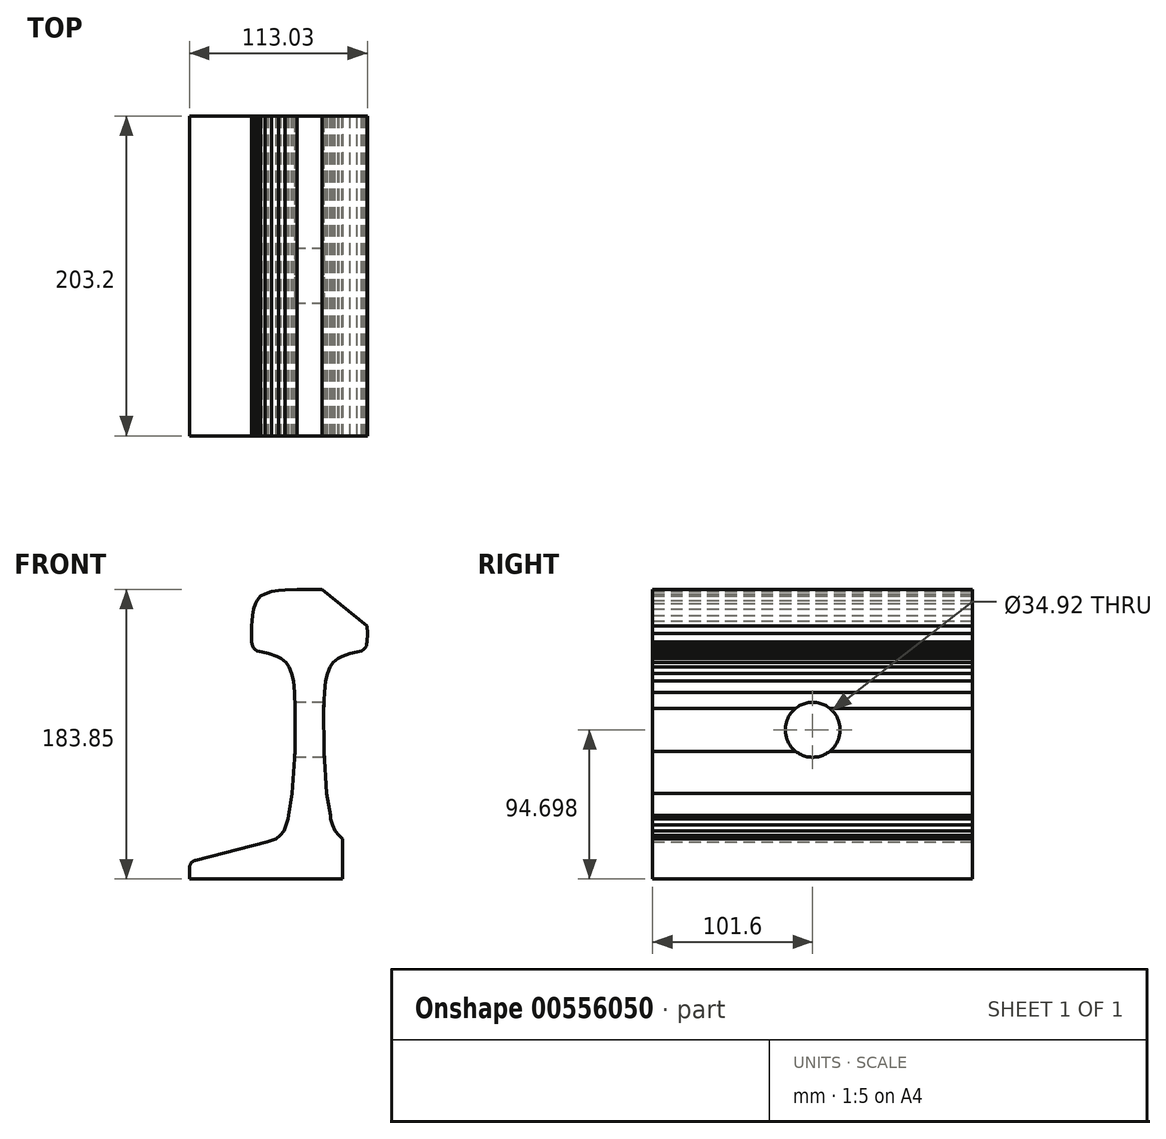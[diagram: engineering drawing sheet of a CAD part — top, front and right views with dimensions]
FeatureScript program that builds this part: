
annotation { "Feature Type Name" : "Feature", "Feature Type Description" : "" }
export const myFeature = defineFeature(function(context is Context, id is Id, definition is map)
    precondition{}
    {
        {
            var Q0;
            Q0=qCreatedBy(makeId("Front.planeOp"),FACE);
            var sketch = newSketch(context, id + "F0", { "sketchPlane" : qUnion([Q0])});
            skLineSegment(sketch, "E0", {"start": v(-76.2, -57.1) * mm, "end": v(76.2, -57.1) * mm});
            skLineSegment(sketch, "E1", {"start": v(-76.2, -57.1) * mm, "end": v(-76.2, -46.22) * mm});
            skLineSegment(sketch, "E2", {"start": v(-26.84, -33.73) * mm, "end": v(-76.2, -46.22) * mm});
            skPoint(sketch, "E3.startSnap0", {"position": v(0, -57.1) * mm});
            skPoint(sketch, "E3.endSnap0", {"position": v(0, -57.1) * mm});
            skLineSegment(sketch, "E4.MirrorCS", {"start": v(26.84, -33.73) * mm, "end": v(76.2, -46.22) * mm});
            skLineSegment(sketch, "E5.MirrorCS", {"start": v(0, -26.94) * mm, "end": v(0, -26.94) * mm});
            skLineSegment(sketch, "E6.MirrorCS", {"start": v(76.2, -57.1) * mm, "end": v(76.2, -46.22) * mm});
            skLineSegment(sketch, "E7", {"start": v(-26.84, -33.73) * mm, "end": v(-21.16, -31.84) * mm});
            skLineSegment(sketch, "E8", {"start": v(-21.16, -31.84) * mm, "end": v(-18.7, -29.61) * mm});
            skLineSegment(sketch, "E9", {"start": v(-18.7, -29.61) * mm, "end": v(-16.22, -26.55) * mm});
            skLineSegment(sketch, "E10", {"start": v(-16.22, -26.55) * mm, "end": v(-14.69, -22.9) * mm});
            skLineSegment(sketch, "E11", {"start": v(-14.69, -22.9) * mm, "end": v(-13.49, -19.14) * mm});
            skLineSegment(sketch, "E12", {"start": v(-13.49, -19.14) * mm, "end": v(-13.3, -16.85) * mm});
            skLineSegment(sketch, "E13", {"start": v(-13.3, -16.85) * mm, "end": v(-10.94, -2.66) * mm});
            skLineSegment(sketch, "E14", {"start": v(-10.94, -2.66) * mm, "end": v(-9.17, 23.94) * mm});
            skLineSegment(sketch, "E15", {"start": v(-9.17, 23.94) * mm, "end": v(-9.1, 51.27) * mm});
            skLineSegment(sketch, "E16", {"start": v(-9.1, 51.27) * mm, "end": v(-9.47, 61.37) * mm});
            skLineSegment(sketch, "E17", {"start": v(-36.63, 93.52) * mm, "end": v(-36.6, 93.52) * mm});
            skLineSegment(sketch, "E18", {"start": v(-9.47, 61.37) * mm, "end": v(-10.2, 68.53) * mm});
            skLineSegment(sketch, "E19", {"start": v(-10.2, 68.53) * mm, "end": v(-11.42, 73.4) * mm});
            skLineSegment(sketch, "E20", {"start": v(-11.42, 73.4) * mm, "end": v(-12.99, 77.66) * mm});
            skLineSegment(sketch, "E21", {"start": v(-12.99, 77.66) * mm, "end": v(-14.98, 80.45) * mm});
            skLineSegment(sketch, "E22", {"start": v(-14.98, 80.45) * mm, "end": v(-18.1, 83) * mm});
            skLineSegment(sketch, "E23", {"start": v(-18.1, 83) * mm, "end": v(-20.68, 84.15) * mm});
            skLineSegment(sketch, "E24", {"start": v(-20.68, 84.15) * mm, "end": v(-25.92, 85.98) * mm});
            skLineSegment(sketch, "E25", {"start": v(-25.92, 85.98) * mm, "end": v(-30.18, 87.13) * mm});
            skLineSegment(sketch, "E26", {"start": v(-30.18, 87.13) * mm, "end": v(-33.1, 87.75) * mm});
            skLineSegment(sketch, "E27", {"start": v(-33.1, 87.75) * mm, "end": v(-34.18, 88.3) * mm});
            skLineSegment(sketch, "E28", {"start": v(-34.18, 88.3) * mm, "end": v(-35.39, 89.62) * mm});
            skLineSegment(sketch, "E29", {"start": v(-35.39, 89.62) * mm, "end": v(-36.17, 91) * mm});
            skLineSegment(sketch, "E30", {"start": v(-36.17, 91) * mm, "end": v(-36.4, 91.97) * mm});
            skLineSegment(sketch, "E31", {"start": v(-36.4, 91.97) * mm, "end": v(-36.6, 93.51) * mm});
            skLineSegment(sketch, "E32", {"start": v(-36.6, 93.51) * mm, "end": v(-36.83, 98.88) * mm});
            skLineSegment(sketch, "E33", {"start": v(-36.83, 98.88) * mm, "end": v(-36.67, 103.67) * mm});
            skLineSegment(sketch, "E34", {"start": v(-36.67, 103.67) * mm, "end": v(-36.4, 106.65) * mm});
            skLineSegment(sketch, "E35", {"start": v(-36.4, 106.65) * mm, "end": v(-36.18, 110.32) * mm});
            skLineSegment(sketch, "E36", {"start": v(-36.18, 110.32) * mm, "end": v(-35.56, 114.28) * mm});
            skLineSegment(sketch, "E37", {"start": v(-35.56, 114.28) * mm, "end": v(-34.24, 117.98) * mm});
            skLineSegment(sketch, "E38", {"start": v(-34.24, 117.98) * mm, "end": v(-33.33, 119.88) * mm});
            skLineSegment(sketch, "E39", {"start": v(-33.33, 119.88) * mm, "end": v(-31.13, 122.46) * mm});
            skLineSegment(sketch, "E40", {"start": v(-31.13, 122.46) * mm, "end": v(-28.22, 124.04) * mm});
            skLineSegment(sketch, "E41", {"start": v(-28.22, 124.04) * mm, "end": v(-24.03, 125.35) * mm});
            skLineSegment(sketch, "E42", {"start": v(-24.03, 125.35) * mm, "end": v(-19.54, 126) * mm});
            skLineSegment(sketch, "E43.MirrorCS", {"start": v(36.4, 91.97) * mm, "end": v(36.6, 93.51) * mm});
            skLineSegment(sketch, "E44.MirrorCS", {"start": v(36.17, 91) * mm, "end": v(36.4, 91.97) * mm});
            skLineSegment(sketch, "E45.MirrorCS", {"start": v(13.49, -19.14) * mm, "end": v(13.3, -16.85) * mm});
            skLineSegment(sketch, "E46.MirrorCS", {"start": v(36.67, 103.67) * mm, "end": v(36.4, 106.65) * mm});
            skLineSegment(sketch, "E47.MirrorCS", {"start": v(20.68, 84.15) * mm, "end": v(25.92, 85.98) * mm});
            skLineSegment(sketch, "E48.MirrorCS", {"start": v(31.13, 122.46) * mm, "end": v(28.22, 124.04) * mm});
            skLineSegment(sketch, "E49.MirrorCS", {"start": v(36.6, 93.51) * mm, "end": v(36.83, 98.88) * mm});
            skLineSegment(sketch, "E50.MirrorCS", {"start": v(16.22, -26.55) * mm, "end": v(14.69, -22.9) * mm});
            skLineSegment(sketch, "E51.MirrorCS", {"start": v(34.18, 88.3) * mm, "end": v(35.39, 89.62) * mm});
            skLineSegment(sketch, "E52.MirrorCS", {"start": v(14.69, -22.9) * mm, "end": v(13.49, -19.14) * mm});
            skLineSegment(sketch, "E53.MirrorCS", {"start": v(12.99, 77.66) * mm, "end": v(14.98, 80.45) * mm});
            skLineSegment(sketch, "E54.MirrorCS", {"start": v(35.56, 114.28) * mm, "end": v(34.24, 117.98) * mm});
            skLineSegment(sketch, "E55.MirrorCS", {"start": v(28.22, 124.04) * mm, "end": v(24.03, 125.35) * mm});
            skLineSegment(sketch, "E56.MirrorCS", {"start": v(25.92, 85.98) * mm, "end": v(30.18, 87.13) * mm});
            skLineSegment(sketch, "E57.MirrorCS", {"start": v(26.84, -33.73) * mm, "end": v(21.16, -31.84) * mm});
            skLineSegment(sketch, "E58.MirrorCS", {"start": v(18.1, 83) * mm, "end": v(20.68, 84.15) * mm});
            skLineSegment(sketch, "E59.MirrorCS", {"start": v(21.16, -31.84) * mm, "end": v(18.7, -29.61) * mm});
            skLineSegment(sketch, "E60.MirrorCS", {"start": v(14.98, 80.45) * mm, "end": v(18.1, 83) * mm});
            skLineSegment(sketch, "E61.MirrorCS", {"start": v(33.1, 87.75) * mm, "end": v(34.18, 88.3) * mm});
            skLineSegment(sketch, "E62.MirrorCS", {"start": v(33.33, 119.88) * mm, "end": v(31.13, 122.46) * mm});
            skLineSegment(sketch, "E63.MirrorCS", {"start": v(30.18, 87.13) * mm, "end": v(33.1, 87.75) * mm});
            skLineSegment(sketch, "E64.MirrorCS", {"start": v(10.2, 68.53) * mm, "end": v(11.42, 73.4) * mm});
            skLineSegment(sketch, "E65.MirrorCS", {"start": v(34.24, 117.98) * mm, "end": v(33.33, 119.88) * mm});
            skLineSegment(sketch, "E66.MirrorCS", {"start": v(11.42, 73.4) * mm, "end": v(12.99, 77.66) * mm});
            skLineSegment(sketch, "E67.MirrorCS", {"start": v(24.03, 125.35) * mm, "end": v(19.54, 126) * mm});
            skLineSegment(sketch, "E68.MirrorCS", {"start": v(18.7, -29.61) * mm, "end": v(16.22, -26.55) * mm});
            skLineSegment(sketch, "E69.MirrorCS", {"start": v(35.39, 89.62) * mm, "end": v(36.17, 91) * mm});
            skLineSegment(sketch, "E70.MirrorCS", {"start": v(36.18, 110.32) * mm, "end": v(35.56, 114.28) * mm});
            skLineSegment(sketch, "E71.MirrorCS", {"start": v(36.4, 106.65) * mm, "end": v(36.18, 110.32) * mm});
            skLineSegment(sketch, "E72.MirrorCS", {"start": v(9.47, 61.37) * mm, "end": v(10.2, 68.53) * mm});
            skLineSegment(sketch, "E73.MirrorCS", {"start": v(15.45, 126.6) * mm, "end": v(15.43, 126.61) * mm});
            skLineSegment(sketch, "E74.MirrorCS", {"start": v(36.83, 98.88) * mm, "end": v(36.67, 103.67) * mm});
            skLineSegment(sketch, "E75.MirrorCS", {"start": v(10.94, -2.66) * mm, "end": v(9.17, 23.94) * mm});
            skLineSegment(sketch, "E76.MirrorCS", {"start": v(9.1, 51.27) * mm, "end": v(9.47, 61.37) * mm});
            skLineSegment(sketch, "E77.MirrorCS", {"start": v(13.3, -16.85) * mm, "end": v(10.94, -2.66) * mm});
            skLineSegment(sketch, "E78.MirrorCS", {"start": v(9.17, 23.94) * mm, "end": v(9.1, 51.27) * mm});
            skPoint(sketch, "E79.start.orphan", {"position": v(-15.43, 126.61) * mm});
            skLineSegment(sketch, "E80", {"start": v(-19.54, 126) * mm, "end": v(-15.43, 126.4) * mm});
            skLineSegment(sketch, "E81", {"start": v(-15.43, 126.4) * mm, "end": v(-8, 126.76) * mm});
            skLineSegment(sketch, "E82", {"start": v(-8, 126.76) * mm, "end": v(0, 126.76) * mm});
            skLineSegment(sketch, "E83.MirrorCS", {"start": v(8, 126.76) * mm, "end": v(0, 126.76) * mm});
            skLineSegment(sketch, "E84.MirrorCS", {"start": v(15.43, 126.4) * mm, "end": v(8, 126.76) * mm});
            skLineSegment(sketch, "E85.MirrorCS", {"start": v(19.54, 126) * mm, "end": v(15.43, 126.4) * mm});
            skPoint(sketch, "E86.orphan", {"position": v(-76.2, -26.94) * mm});
            skPoint(sketch, "E87.orphan", {"position": v(-31.72, -14.5) * mm});
            skPoint(sketch, "E88.end.orphan", {"position": v(-76.21, 41.14) * mm});
            skPoint(sketch, "E88.start.orphan", {"position": v(-76.21, -8.79) * mm});
            skLineSegment(sketch, "E89", {"start": v(76.2, -57.1) * mm, "end": v(76.2, -57.1) * mm});
            skPoint(sketch, "E90.orphan", {"position": v(76.2, -26.94) * mm});
            skPoint(sketch, "E91.MirrorCS.end.orphan", {"position": v(76.21, -8.79) * mm});
            skPoint(sketch, "E91.MirrorCS.start.orphan", {"position": v(31.72, -14.5) * mm});
            skPoint(sketch, "E92.orphan", {"position": v(0, -26.94) * mm});
            skLineSegment(sketch, "E93.trimOffspring", {"start": v(36.6, 93.52) * mm, "end": v(37.03, 93.52) * mm});
            skPoint(sketch, "E94.trimOffspring.end.orphan", {"position": v(0, 152.1) * mm});
            skPoint(sketch, "E3.start.orphan", {"position": v(0, -57.1) * mm});
            skSolve(sketch);
        }
        {
            var Q0;
            Q0=qSketchRegion(id+"F0",true);
            extrude(context, id + "F1", {"entities" : qUnion([Q0]), "depth" : 203.2 * mm, "offsetDistance" : 25.4 * mm});
        }
        {
            var Q0;
            Q0=makeQuery(id+"F1.opExtrude","SWEPT_EDGE",EDGE,{"disambiguationData":[OSD([sQuery(id+"F0.wireOp",EDGE,"E4.MirrorCS"),sQuery(id+"F0.wireOp",EDGE,"E6.MirrorCS")])]});
            var Q1;
            Q1=makeQuery(id+"F1.opExtrude","SWEPT_EDGE",EDGE,{"disambiguationData":[OSD([sQuery(id+"F0.wireOp",EDGE,"E1"),sQuery(id+"F0.wireOp",EDGE,"E2")])]});
            fillet(context, id + "F2", {"entities" : qUnion([Q0, Q1]), "radius" : 5.08 * mm, "tangentPropagation" : true, "allowEdgeOverflow" : false});
        }
        {
            var Q0;
            Q0=makeQuery(id+"F1.opExtrude","CAP_FACE",FACE,{"disambiguationData":[OSD([sQuery(id+"F0.wireOp",EDGE,"E0"),sQuery(id+"F0.wireOp",EDGE,"E1"),sQuery(id+"F0.wireOp",EDGE,"E2"),sQuery(id+"F0.wireOp",EDGE,"E4.MirrorCS"),sQuery(id+"F0.wireOp",EDGE,"E7"),sQuery(id+"F0.wireOp",EDGE,"E8"),sQuery(id+"F0.wireOp",EDGE,"E9"),sQuery(id+"F0.wireOp",EDGE,"E10"),sQuery(id+"F0.wireOp",EDGE,"E11"),sQuery(id+"F0.wireOp",EDGE,"E12"),sQuery(id+"F0.wireOp",EDGE,"E13"),sQuery(id+"F0.wireOp",EDGE,"E14"),sQuery(id+"F0.wireOp",EDGE,"E15"),sQuery(id+"F0.wireOp",EDGE,"E16"),sQuery(id+"F0.wireOp",EDGE,"E18"),sQuery(id+"F0.wireOp",EDGE,"E19"),sQuery(id+"F0.wireOp",EDGE,"E20"),sQuery(id+"F0.wireOp",EDGE,"E21"),sQuery(id+"F0.wireOp",EDGE,"E22"),sQuery(id+"F0.wireOp",EDGE,"E23"),sQuery(id+"F0.wireOp",EDGE,"E24"),sQuery(id+"F0.wireOp",EDGE,"E25"),sQuery(id+"F0.wireOp",EDGE,"E26"),sQuery(id+"F0.wireOp",EDGE,"E27"),sQuery(id+"F0.wireOp",EDGE,"E28"),sQuery(id+"F0.wireOp",EDGE,"E29"),sQuery(id+"F0.wireOp",EDGE,"E30"),sQuery(id+"F0.wireOp",EDGE,"E31"),sQuery(id+"F0.wireOp",EDGE,"E32"),sQuery(id+"F0.wireOp",EDGE,"E33"),sQuery(id+"F0.wireOp",EDGE,"E34"),sQuery(id+"F0.wireOp",EDGE,"E35"),sQuery(id+"F0.wireOp",EDGE,"E36"),sQuery(id+"F0.wireOp",EDGE,"E37"),sQuery(id+"F0.wireOp",EDGE,"E38"),sQuery(id+"F0.wireOp",EDGE,"E39"),sQuery(id+"F0.wireOp",EDGE,"E40"),sQuery(id+"F0.wireOp",EDGE,"E41"),sQuery(id+"F0.wireOp",EDGE,"E42"),sQuery(id+"F0.wireOp",EDGE,"E43.MirrorCS"),sQuery(id+"F0.wireOp",EDGE,"E44.MirrorCS"),sQuery(id+"F0.wireOp",EDGE,"E45.MirrorCS"),sQuery(id+"F0.wireOp",EDGE,"E46.MirrorCS"),sQuery(id+"F0.wireOp",EDGE,"E47.MirrorCS"),sQuery(id+"F0.wireOp",EDGE,"E48.MirrorCS"),sQuery(id+"F0.wireOp",EDGE,"E49.MirrorCS"),sQuery(id+"F0.wireOp",EDGE,"E50.MirrorCS"),sQuery(id+"F0.wireOp",EDGE,"E51.MirrorCS"),sQuery(id+"F0.wireOp",EDGE,"E52.MirrorCS"),sQuery(id+"F0.wireOp",EDGE,"E53.MirrorCS"),sQuery(id+"F0.wireOp",EDGE,"E54.MirrorCS"),sQuery(id+"F0.wireOp",EDGE,"E55.MirrorCS"),sQuery(id+"F0.wireOp",EDGE,"E56.MirrorCS"),sQuery(id+"F0.wireOp",EDGE,"E57.MirrorCS"),sQuery(id+"F0.wireOp",EDGE,"E58.MirrorCS"),sQuery(id+"F0.wireOp",EDGE,"E59.MirrorCS"),sQuery(id+"F0.wireOp",EDGE,"E60.MirrorCS"),sQuery(id+"F0.wireOp",EDGE,"E61.MirrorCS"),sQuery(id+"F0.wireOp",EDGE,"E62.MirrorCS"),sQuery(id+"F0.wireOp",EDGE,"E63.MirrorCS"),sQuery(id+"F0.wireOp",EDGE,"E64.MirrorCS"),sQuery(id+"F0.wireOp",EDGE,"E65.MirrorCS"),sQuery(id+"F0.wireOp",EDGE,"E66.MirrorCS"),sQuery(id+"F0.wireOp",EDGE,"E67.MirrorCS"),sQuery(id+"F0.wireOp",EDGE,"E68.MirrorCS"),sQuery(id+"F0.wireOp",EDGE,"E69.MirrorCS"),sQuery(id+"F0.wireOp",EDGE,"E70.MirrorCS"),sQuery(id+"F0.wireOp",EDGE,"E71.MirrorCS"),sQuery(id+"F0.wireOp",EDGE,"E72.MirrorCS"),sQuery(id+"F0.wireOp",EDGE,"E74.MirrorCS"),sQuery(id+"F0.wireOp",EDGE,"E75.MirrorCS"),sQuery(id+"F0.wireOp",EDGE,"E6.MirrorCS"),sQuery(id+"F0.wireOp",EDGE,"E76.MirrorCS"),sQuery(id+"F0.wireOp",EDGE,"E77.MirrorCS"),sQuery(id+"F0.wireOp",EDGE,"E78.MirrorCS"),sQuery(id+"F0.wireOp",EDGE,"E80"),sQuery(id+"F0.wireOp",EDGE,"E81"),sQuery(id+"F0.wireOp",EDGE,"E82"),sQuery(id+"F0.wireOp",EDGE,"E83.MirrorCS"),sQuery(id+"F0.wireOp",EDGE,"E84.MirrorCS"),sQuery(id+"F0.wireOp",EDGE,"E85.MirrorCS")])],"isStart":false});
            var sketch = newSketch(context, id + "F3", { "sketchPlane" : qUnion([Q0])});
            skLineSegment(sketch, "E95", {"start": v(21.16, -31.84) * mm, "end": v(21.16, -57.1) * mm});
            skSolve(sketch);
        }
        {
            var Q0;
            {var subQ4=sQuery(id+"F3.wireOp",EDGE,"E95");Q0=makeQuery(id+"F3.imprint","IMPRINT",FACE,{"disambiguationData":[TD([[makeQuery(id+"F3.imprint","IMPRINT",EDGE,{"derivedFrom":subQ4}),1.0]])]});}
            extrude(context, id + "F4", {"entities" : qUnion([Q0]), "operationType" : NewBodyOperationType.REMOVE, "oppositeDirection" : true, "depth" : 508 * mm, "offsetDistance" : 25.4 * mm});
        }
        {
            var Q0;
            Q0=qCreatedBy(makeId("Right.planeOp"),FACE);
            var sketch = newSketch(context, id + "F5", { "sketchPlane" : qUnion([Q0])});
            skPoint(sketch, "E96.centerSnap0", {"position": v(0, 37.6) * mm});
            skPoint(sketch, "E96.centerSnap1", {"position": v(-101.6, 23.94) * mm});
            skCircle(sketch, "E97", {"center": v(-101.6, 37.6) * mm, "radius": 17.46 * mm});
            skSolve(sketch);
        }
        {
            var Q0;
            Q0 = qSketchRegion(id + "F5", true);
            extrude(context, id + "F6", {"entities" : qUnion([Q0]), "operationType" : NewBodyOperationType.REMOVE, "endBound" : BoundingType.SYMMETRIC, "depth" : 304.8 * mm, "offsetDistance" : 25.4 * mm});
        }
        {
            var Q0;
            Q0=makeQuery(id+"F1.opExtrude","CAP_FACE",FACE,{"disambiguationData":[OSD([sQuery(id+"F0.wireOp",EDGE,"E0"),sQuery(id+"F0.wireOp",EDGE,"E1"),sQuery(id+"F0.wireOp",EDGE,"E2"),sQuery(id+"F0.wireOp",EDGE,"E4.MirrorCS"),sQuery(id+"F0.wireOp",EDGE,"E7"),sQuery(id+"F0.wireOp",EDGE,"E8"),sQuery(id+"F0.wireOp",EDGE,"E9"),sQuery(id+"F0.wireOp",EDGE,"E10"),sQuery(id+"F0.wireOp",EDGE,"E11"),sQuery(id+"F0.wireOp",EDGE,"E12"),sQuery(id+"F0.wireOp",EDGE,"E13"),sQuery(id+"F0.wireOp",EDGE,"E14"),sQuery(id+"F0.wireOp",EDGE,"E15"),sQuery(id+"F0.wireOp",EDGE,"E16"),sQuery(id+"F0.wireOp",EDGE,"E18"),sQuery(id+"F0.wireOp",EDGE,"E19"),sQuery(id+"F0.wireOp",EDGE,"E20"),sQuery(id+"F0.wireOp",EDGE,"E21"),sQuery(id+"F0.wireOp",EDGE,"E22"),sQuery(id+"F0.wireOp",EDGE,"E23"),sQuery(id+"F0.wireOp",EDGE,"E24"),sQuery(id+"F0.wireOp",EDGE,"E25"),sQuery(id+"F0.wireOp",EDGE,"E26"),sQuery(id+"F0.wireOp",EDGE,"E27"),sQuery(id+"F0.wireOp",EDGE,"E28"),sQuery(id+"F0.wireOp",EDGE,"E29"),sQuery(id+"F0.wireOp",EDGE,"E30"),sQuery(id+"F0.wireOp",EDGE,"E31"),sQuery(id+"F0.wireOp",EDGE,"E32"),sQuery(id+"F0.wireOp",EDGE,"E33"),sQuery(id+"F0.wireOp",EDGE,"E34"),sQuery(id+"F0.wireOp",EDGE,"E35"),sQuery(id+"F0.wireOp",EDGE,"E36"),sQuery(id+"F0.wireOp",EDGE,"E37"),sQuery(id+"F0.wireOp",EDGE,"E38"),sQuery(id+"F0.wireOp",EDGE,"E39"),sQuery(id+"F0.wireOp",EDGE,"E40"),sQuery(id+"F0.wireOp",EDGE,"E41"),sQuery(id+"F0.wireOp",EDGE,"E42"),sQuery(id+"F0.wireOp",EDGE,"E43.MirrorCS"),sQuery(id+"F0.wireOp",EDGE,"E44.MirrorCS"),sQuery(id+"F0.wireOp",EDGE,"E45.MirrorCS"),sQuery(id+"F0.wireOp",EDGE,"E46.MirrorCS"),sQuery(id+"F0.wireOp",EDGE,"E47.MirrorCS"),sQuery(id+"F0.wireOp",EDGE,"E48.MirrorCS"),sQuery(id+"F0.wireOp",EDGE,"E49.MirrorCS"),sQuery(id+"F0.wireOp",EDGE,"E50.MirrorCS"),sQuery(id+"F0.wireOp",EDGE,"E51.MirrorCS"),sQuery(id+"F0.wireOp",EDGE,"E52.MirrorCS"),sQuery(id+"F0.wireOp",EDGE,"E53.MirrorCS"),sQuery(id+"F0.wireOp",EDGE,"E54.MirrorCS"),sQuery(id+"F0.wireOp",EDGE,"E55.MirrorCS"),sQuery(id+"F0.wireOp",EDGE,"E56.MirrorCS"),sQuery(id+"F0.wireOp",EDGE,"E57.MirrorCS"),sQuery(id+"F0.wireOp",EDGE,"E58.MirrorCS"),sQuery(id+"F0.wireOp",EDGE,"E59.MirrorCS"),sQuery(id+"F0.wireOp",EDGE,"E60.MirrorCS"),sQuery(id+"F0.wireOp",EDGE,"E61.MirrorCS"),sQuery(id+"F0.wireOp",EDGE,"E62.MirrorCS"),sQuery(id+"F0.wireOp",EDGE,"E63.MirrorCS"),sQuery(id+"F0.wireOp",EDGE,"E64.MirrorCS"),sQuery(id+"F0.wireOp",EDGE,"E65.MirrorCS"),sQuery(id+"F0.wireOp",EDGE,"E66.MirrorCS"),sQuery(id+"F0.wireOp",EDGE,"E67.MirrorCS"),sQuery(id+"F0.wireOp",EDGE,"E68.MirrorCS"),sQuery(id+"F0.wireOp",EDGE,"E69.MirrorCS"),sQuery(id+"F0.wireOp",EDGE,"E70.MirrorCS"),sQuery(id+"F0.wireOp",EDGE,"E71.MirrorCS"),sQuery(id+"F0.wireOp",EDGE,"E72.MirrorCS"),sQuery(id+"F0.wireOp",EDGE,"E74.MirrorCS"),sQuery(id+"F0.wireOp",EDGE,"E75.MirrorCS"),sQuery(id+"F0.wireOp",EDGE,"E6.MirrorCS"),sQuery(id+"F0.wireOp",EDGE,"E76.MirrorCS"),sQuery(id+"F0.wireOp",EDGE,"E77.MirrorCS"),sQuery(id+"F0.wireOp",EDGE,"E78.MirrorCS"),sQuery(id+"F0.wireOp",EDGE,"E80"),sQuery(id+"F0.wireOp",EDGE,"E81"),sQuery(id+"F0.wireOp",EDGE,"E82"),sQuery(id+"F0.wireOp",EDGE,"E83.MirrorCS"),sQuery(id+"F0.wireOp",EDGE,"E84.MirrorCS"),sQuery(id+"F0.wireOp",EDGE,"E85.MirrorCS")])],"isStart":false});
            var sketch = newSketch(context, id + "F7", { "sketchPlane" : qUnion([Q0])});
            skLineSegment(sketch, "E98", {"start": v(8, 126.76) * mm, "end": v(36.67, 103.67) * mm});
            skSolve(sketch);
        }
        {
            var Q0;
            Q0 = qSketchRegion(id + "F7", true);
            var Q1;
            Q1=makeQuery(id+"F7.imprint","IMPRINT",FACE,{"disambiguationData":[TD([[makeQuery(id+"F7.imprint","IMPRINT",EDGE,{"derivedFrom":sQuery(id+"F7.wireOp",EDGE,"E98")}),1.0]])]});
            extrude(context, id + "F8", {"entities" : qUnion([Q0, Q1]), "operationType" : NewBodyOperationType.REMOVE, "oppositeDirection" : true, "depth" : 508 * mm, "offsetDistance" : 25.4 * mm});
        }
    });
